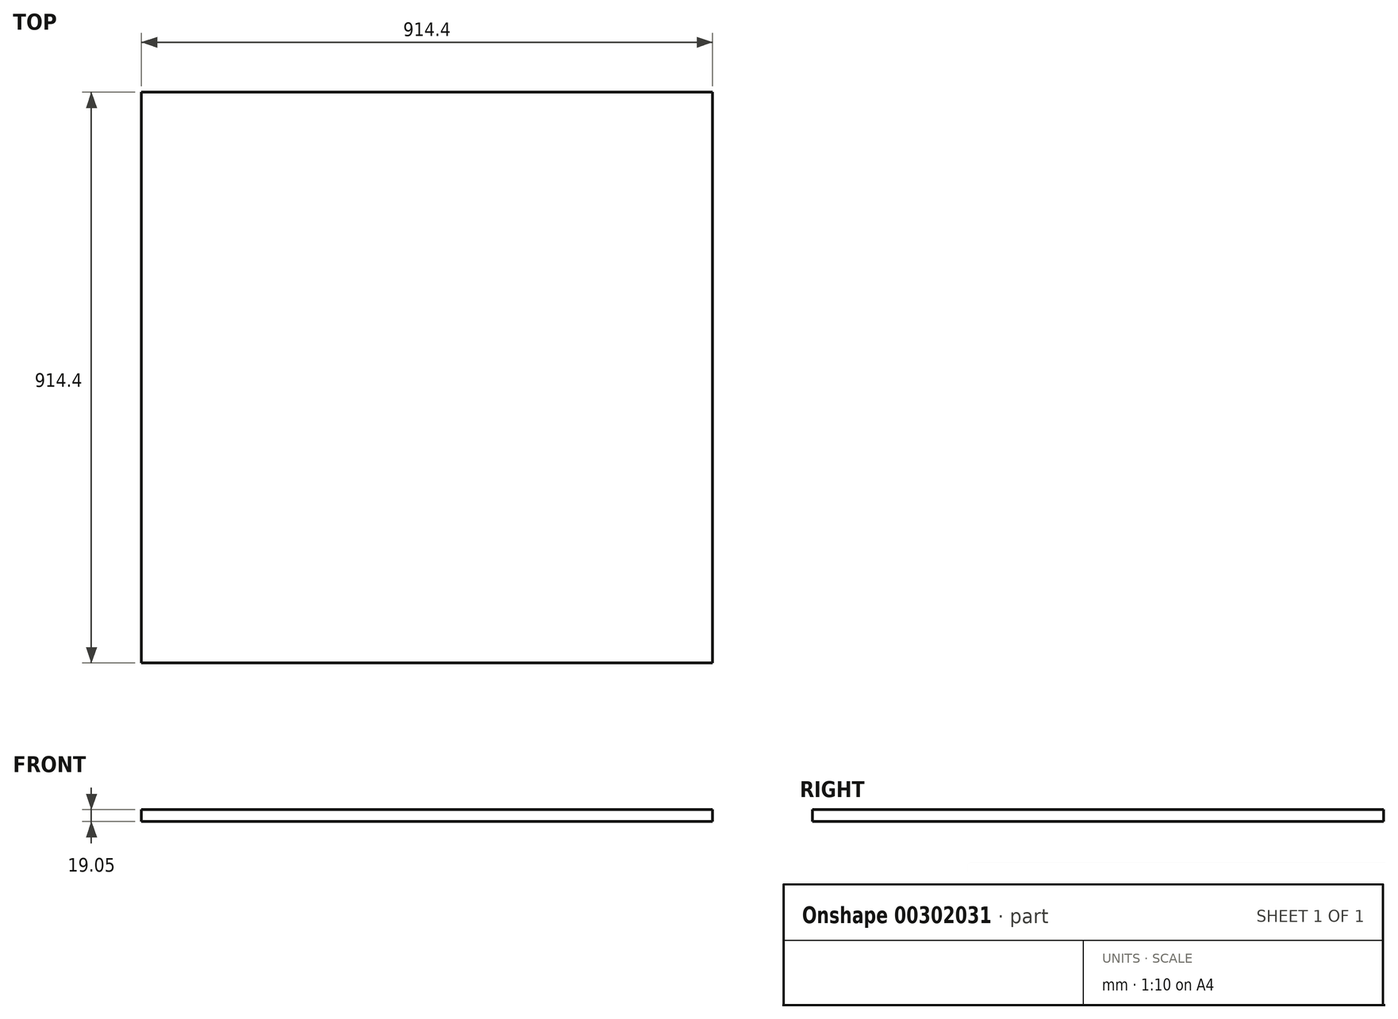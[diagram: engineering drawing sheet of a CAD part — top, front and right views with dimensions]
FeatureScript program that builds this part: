
annotation { "Feature Type Name" : "Feature", "Feature Type Description" : "" }
export const myFeature = defineFeature(function(context is Context, id is Id, definition is map)
    precondition{}
    {
        {
            var Q0;
            Q0=qCreatedBy(makeId("Top.planeOp"),FACE);
            var sketch = newSketch(context, id + "F0", { "sketchPlane" : qUnion([Q0])});
            skLineSegment(sketch, "E0.bottom", {"start": v(457.2, 457.2) * mm, "end": v(-457.2, 457.2) * mm});
            skLineSegment(sketch, "E0.top", {"start": v(457.2, -457.2) * mm, "end": v(-457.2, -457.2) * mm});
            skLineSegment(sketch, "E0.left", {"start": v(457.2, 457.2) * mm, "end": v(457.2, -457.2) * mm});
            skLineSegment(sketch, "E0.right", {"start": v(-457.2, 457.2) * mm, "end": v(-457.2, -457.2) * mm});
            skPoint(sketch, "E0.middle", {"position": v(0, 0) * mm});
            skSolve(sketch);
        }
        {
            var Q0;
            Q0 = qSketchRegion(id + "F0", true);
            extrude(context, id + "F1", {"entities" : qUnion([Q0]), "depth" : 19.05 * mm});
        }
    });
